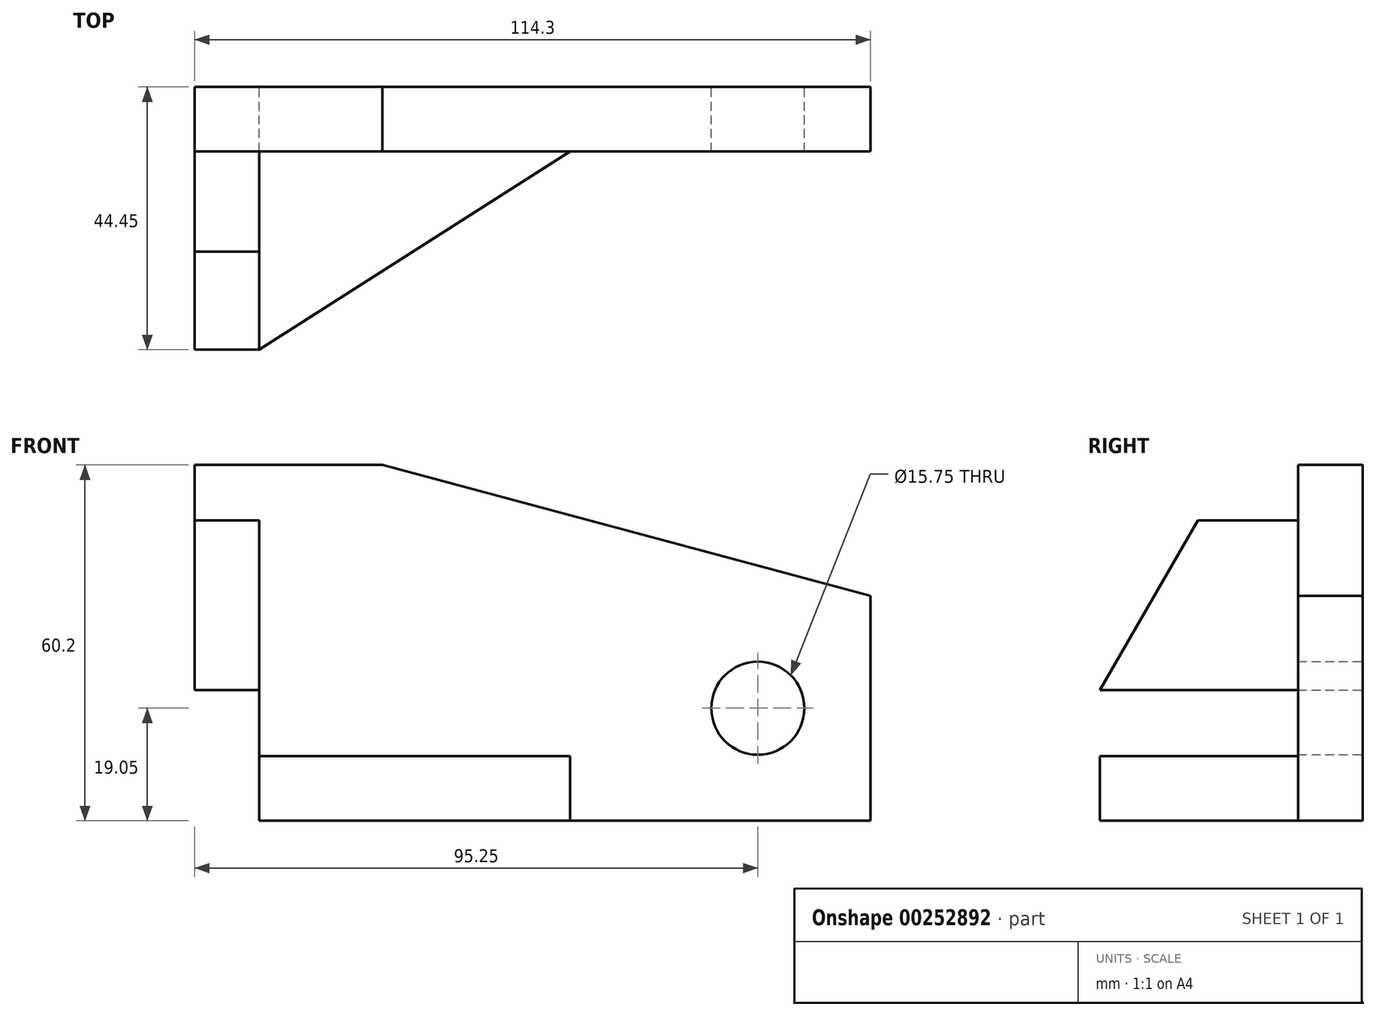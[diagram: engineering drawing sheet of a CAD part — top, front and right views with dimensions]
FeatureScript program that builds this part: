
annotation { "Feature Type Name" : "Feature", "Feature Type Description" : "" }
export const myFeature = defineFeature(function(context is Context, id is Id, definition is map)
    precondition{}
    {
        {
            var Q0;
            Q0=qCreatedBy(makeId("Front.planeOp"),FACE);
            var sketch = newSketch(context, id + "F0", { "sketchPlane" : qUnion([Q0])});
            skLineSegment(sketch, "E0.bottom", {"start": v(0, 60.2) * mm, "end": v(31.75, 60.2) * mm});
            skLineSegment(sketch, "E0.left", {"start": v(0, 60.2) * mm, "end": v(0, 0) * mm});
            skLineSegment(sketch, "E1.bottom", {"start": v(0, 0) * mm, "end": v(114.3, 0) * mm});
            skLineSegment(sketch, "E1.top", {"start": v(0, 22.1) * mm, "end": v(10.92, 22.1) * mm});
            skLineSegment(sketch, "E1.left", {"start": v(0, 0) * mm, "end": v(0, 22.1) * mm});
            skLineSegment(sketch, "E2.top", {"start": v(0, 50.8) * mm, "end": v(10.92, 50.8) * mm});
            skLineSegment(sketch, "E2.left", {"start": v(0, 22.1) * mm, "end": v(0, 50.8) * mm});
            skLineSegment(sketch, "E2.right", {"start": v(10.92, 0) * mm, "end": v(10.92, 50.8) * mm});
            skLineSegment(sketch, "E3.top", {"start": v(10.92, 10.92) * mm, "end": v(63.5, 10.92) * mm});
            skLineSegment(sketch, "E3.right", {"start": v(63.5, 0) * mm, "end": v(63.5, 10.92) * mm});
            skLineSegment(sketch, "E4.bottom", {"start": v(31.75, 60.2) * mm, "end": v(114.3, 38.08) * mm});
            skLineSegment(sketch, "E4.right", {"start": v(114.3, 38.08) * mm, "end": v(114.3, 0) * mm});
            skCircle(sketch, "E5", {"center": v(95.25, 19.05) * mm, "radius": 7.87 * mm});
            skLineSegment(sketch, "E6", {"start": v(95.25, 19.05) * mm, "end": v(95.25, 0) * mm, "construction": true});
            skLineSegment(sketch, "E7", {"start": v(95.25, 19.05) * mm, "end": v(114.3, 19.05) * mm, "construction": true});
            skSolve(sketch);
        }
        {
            var Q0;
            Q0=makeQuery(id+"F0.imprint","IMPRINT",FACE,{"disambiguationData":[TD([[makeQuery(id+"F0.imprint","IMPRINT",EDGE,{"derivedFrom":sQuery(id+"F0.wireOp",EDGE,"E0.bottom")}),-1.0]])]});
            extrude(context, id + "F1", {"entities" : qUnion([Q0]), "depth" : 10.92 * mm});
        }
        {
            var Q0;
            {var subQ0=sQuery(id+"F0.wireOp",EDGE,"E1.top");Q0=makeQuery(id+"F0.imprint","IMPRINT",FACE,{"disambiguationData":[TD([[makeQuery(id+"F0.imprint","IMPRINT",EDGE,{"derivedFrom":subQ0}),1.0]])]});}
            var Q1;
            {var subQ1=sQuery(id+"F0.wireOp",EDGE,"E1.bottom");Q1=makeQuery(id+"F0.imprint","IMPRINT",FACE,{"disambiguationData":[TD([[makeQuery(id+"F0.imprint","IMPRINT",EDGE,{"derivedFrom":subQ1}),1.0]])]});}
            var Q2;
            {var subQ2=sQuery(id+"F0.wireOp",EDGE,"E3.bottom");Q2=makeQuery(id+"F0.imprint","IMPRINT",FACE,{"disambiguationData":[TD([[makeQuery(id+"F0.imprint","IMPRINT",EDGE,{"derivedFrom":subQ2}),1.0]])]});}
            var Q3;
            {var subQ4=sQuery(id+"F0.wireOp",EDGE,"E1.left");Q3=makeQuery(id+"F0.imprint","IMPRINT",FACE,{"disambiguationData":[TD([[makeQuery(id+"F0.imprint","IMPRINT",EDGE,{"derivedFrom":subQ4}),-1.0]])]});}
            extrude(context, id + "F2", {"entities" : qUnion([Q0, Q1, Q2, Q3]), "operationType" : NewBodyOperationType.ADD, "depth" : 44.45 * mm});
        }
        {
            var Q0;
            Q0=qCreatedBy(makeId("Top.planeOp"),FACE);
            var sketch = newSketch(context, id + "F3", { "sketchPlane" : qUnion([Q0])});
            skLineSegment(sketch, "E8", {"start": v(10.92, -44.45) * mm, "end": v(63.5, -10.92) * mm});
            skLineSegment(sketch, "E9", {"start": v(10.92, -44.45) * mm, "end": v(65.81, -47.12) * mm});
            skLineSegment(sketch, "E10", {"start": v(65.81, -47.12) * mm, "end": v(63.5, -10.92) * mm});
            skSolve(sketch);
        }
        {
            var Q0;
            Q0=makeQuery(id+"F3.imprint","IMPRINT",FACE,{"disambiguationData":[TD([[makeQuery(id+"F3.imprint","IMPRINT",EDGE,{"derivedFrom":sQuery(id+"F3.wireOp",EDGE,"E8")}),-1.0]])]});
            extrude(context, id + "F4", {"entities" : qUnion([Q0]), "operationType" : NewBodyOperationType.REMOVE, "depth" : 25.4 * mm});
        }
        {
            var Q0;
            Q0=qCreatedBy(makeId("Right.planeOp"),FACE);
            var sketch = newSketch(context, id + "F5", { "sketchPlane" : qUnion([Q0])});
            skLineSegment(sketch, "E11", {"start": v(-44.45, 22.1) * mm, "end": v(-27.88, 50.8) * mm});
            skLineSegment(sketch, "E12", {"start": v(-44.45, 22.1) * mm, "end": v(-44.45, 0) * mm, "construction": true});
            skLineSegment(sketch, "E13", {"start": v(-44.45, 22.1) * mm, "end": v(-44.45, 50.8) * mm});
            skLineSegment(sketch, "E14", {"start": v(-44.45, 50.8) * mm, "end": v(-27.88, 50.8) * mm});
            skSolve(sketch);
        }
        {
            var Q0;
            Q0=makeQuery(id+"F5.imprint","IMPRINT",FACE,{"disambiguationData":[TD([[makeQuery(id+"F5.imprint","IMPRINT",EDGE,{"derivedFrom":sQuery(id+"F5.wireOp",EDGE,"E11")}),1.0]])]});
            extrude(context, id + "F6", {"entities" : qUnion([Q0]), "operationType" : NewBodyOperationType.REMOVE, "depth" : 39.37 * mm});
        }
    });
